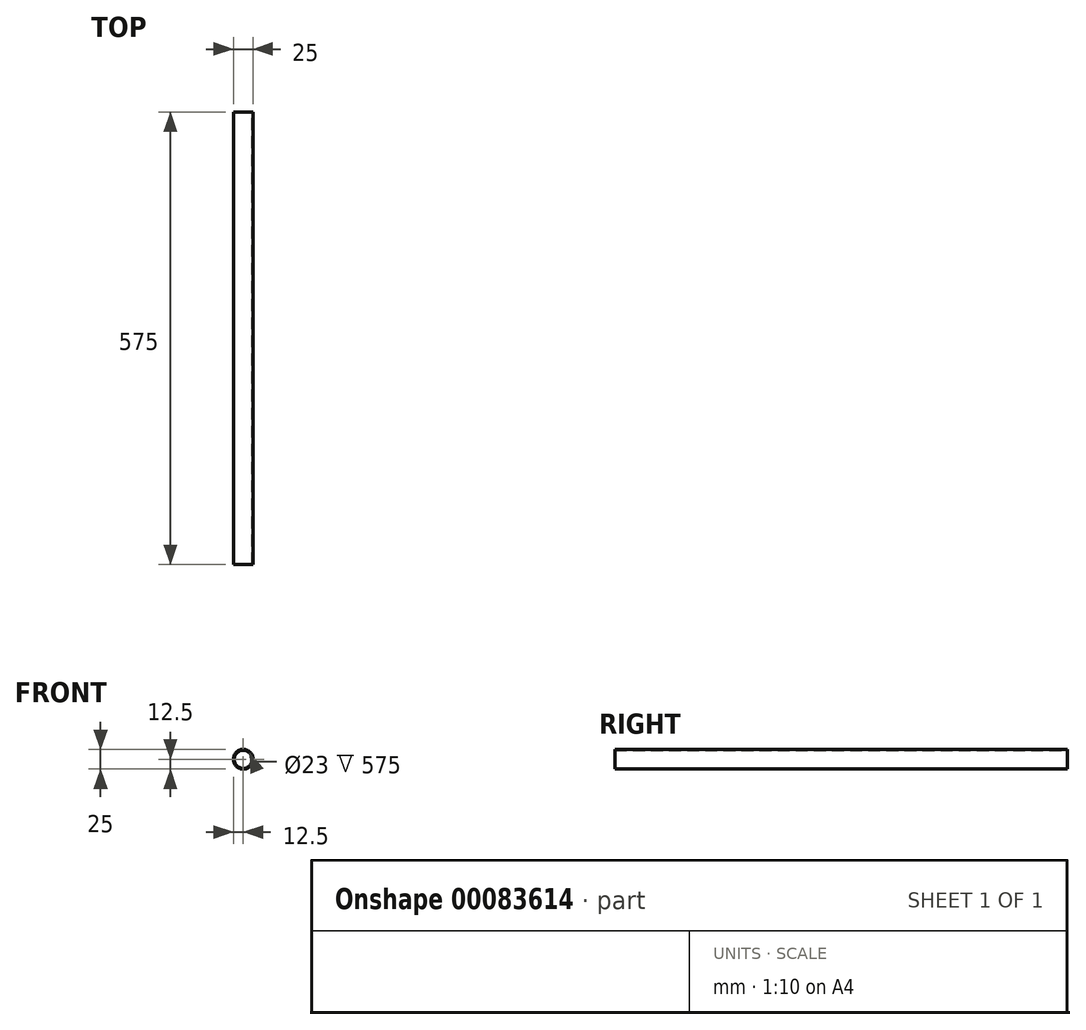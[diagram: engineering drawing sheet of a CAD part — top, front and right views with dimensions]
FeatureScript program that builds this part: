
annotation { "Feature Type Name" : "Feature", "Feature Type Description" : "" }
export const myFeature = defineFeature(function(context is Context, id is Id, definition is map)
    precondition{}
    {
        {
            var Q0;
            Q0=qCreatedBy(makeId("Front.planeOp"),FACE);
            var sketch = newSketch(context, id + "F0", { "sketchPlane" : qUnion([Q0])});
            skCircle(sketch, "E0", {"center": v(0, 0) * mm, "radius": 11.5 * mm});
            skCircle(sketch, "E1", {"center": v(0, 0) * mm, "radius": 12.5 * mm});
            skSolve(sketch);
        }
        {
            var Q0;
            Q0=makeQuery(id+"F0.imprint","IMPRINT",FACE,{"disambiguationData":[TD([[makeQuery(id+"F0.imprint","IMPRINT",EDGE,{"derivedFrom":sQuery(id+"F0.wireOp",EDGE,"E0")}),-1.0]])]});
            extrude(context, id + "F1", {"entities" : qUnion([Q0]), "depth" : 575 * mm});
        }
    });
